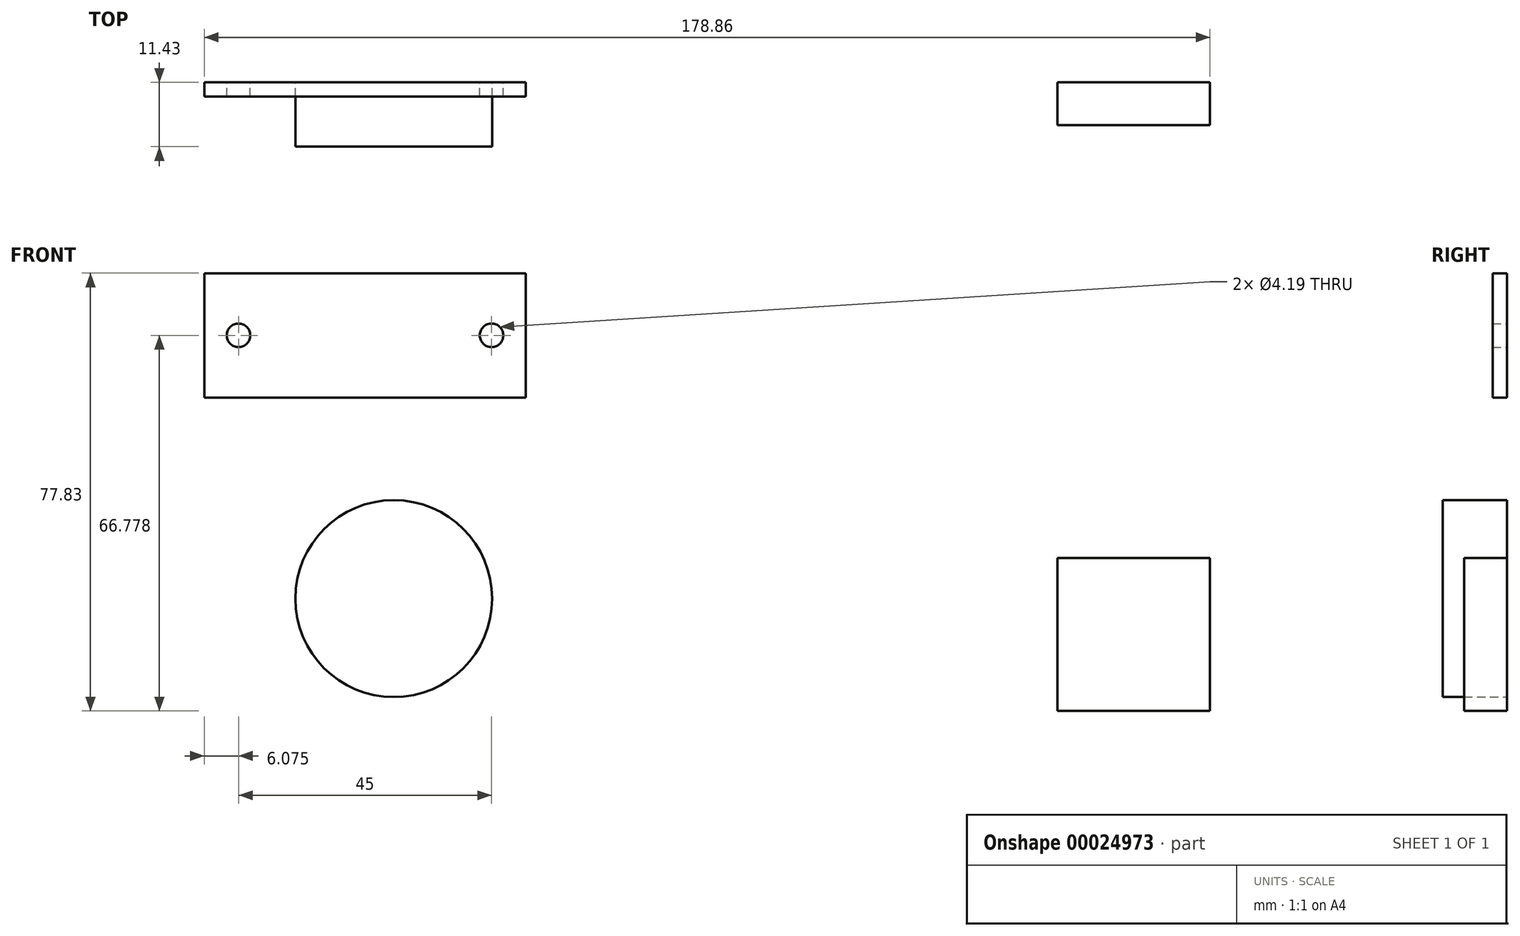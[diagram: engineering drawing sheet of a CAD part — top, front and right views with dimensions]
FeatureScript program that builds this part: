
annotation { "Feature Type Name" : "Feature", "Feature Type Description" : "" }
export const myFeature = defineFeature(function(context is Context, id is Id, definition is map)
    precondition{}
    {
        {
            var Q0;
            Q0=qCreatedBy(makeId("Front.planeOp"),FACE);
            var sketch = newSketch(context, id + "F0", { "sketchPlane" : qUnion([Q0])});
            skCircle(sketch, "E0", {"center": v(-81.58, 15.33) * mm, "radius": 17.5 * mm});
            skLineSegment(sketch, "E1.bottom", {"start": v(-115.26, 73.19) * mm, "end": v(-58.1, 73.19) * mm});
            skLineSegment(sketch, "E1.top", {"start": v(-115.26, 51.09) * mm, "end": v(-58.1, 51.09) * mm});
            skLineSegment(sketch, "E1.left", {"start": v(-115.26, 73.19) * mm, "end": v(-115.26, 51.09) * mm});
            skLineSegment(sketch, "E1.right", {"start": v(-58.1, 73.19) * mm, "end": v(-58.1, 51.09) * mm});
            skLineSegment(sketch, "E2.bottom", {"start": v(36.42, 22.54) * mm, "end": v(63.6, 22.54) * mm});
            skLineSegment(sketch, "E2.top", {"start": v(36.42, -4.64) * mm, "end": v(63.6, -4.64) * mm});
            skLineSegment(sketch, "E2.left", {"start": v(36.42, 22.54) * mm, "end": v(36.42, -4.64) * mm});
            skLineSegment(sketch, "E2.right", {"start": v(63.6, 22.54) * mm, "end": v(63.6, -4.64) * mm});
            skCircle(sketch, "E3", {"center": v(-109.18, 62.14) * mm, "radius": 2.1 * mm});
            skCircle(sketch, "E4", {"center": v(-64.18, 62.14) * mm, "radius": 2.1 * mm});
            skPoint(sketch, "E5", {"position": v(-86.68, 62.14) * mm});
            skSolve(sketch);
        }
        {
            var Q0;
            Q0=makeQuery(id+"F0.imprint","IMPRINT",FACE,{"disambiguationData":[TD([[makeQuery(id+"F0.imprint","IMPRINT",EDGE,{"derivedFrom":sQuery(id+"F0.wireOp",EDGE,"E0")}),1.0]])]});
            extrude(context, id + "F1", {"entities" : qUnion([Q0]), "depth" : 11.43 * mm});
        }
        {
            var Q0;
            Q0=makeQuery(id+"F0.imprint","IMPRINT",FACE,{"disambiguationData":[TD([[makeQuery(id+"F0.imprint","IMPRINT",EDGE,{"derivedFrom":sQuery(id+"F0.wireOp",EDGE,"E1.bottom")}),-1.0]])]});
            extrude(context, id + "F2", {"entities" : qUnion([Q0]), "depth" : 2.54 * mm});
        }
        {
            var Q0;
            Q0=makeQuery(id+"F0.imprint","IMPRINT",FACE,{"disambiguationData":[TD([[makeQuery(id+"F0.imprint","IMPRINT",EDGE,{"derivedFrom":sQuery(id+"F0.wireOp",EDGE,"E2.bottom")}),-1.0]])]});
            extrude(context, id + "F3", {"entities" : qUnion([Q0]), "depth" : 7.62 * mm});
        }
    });
